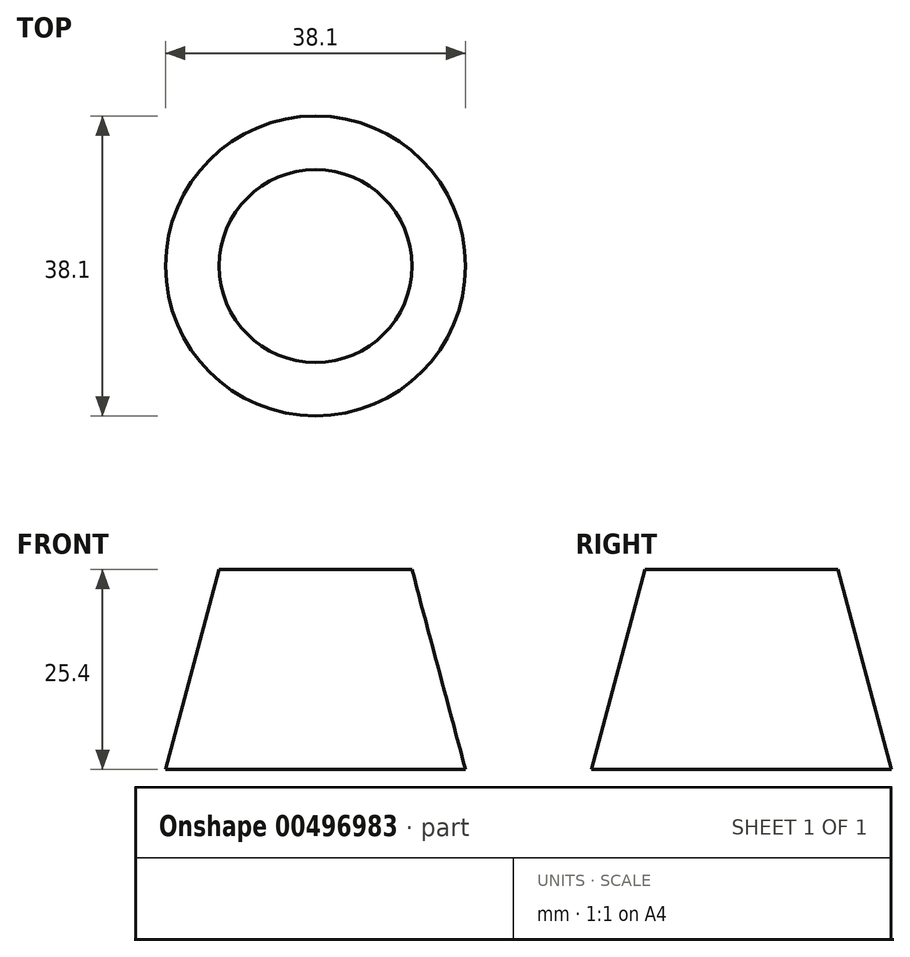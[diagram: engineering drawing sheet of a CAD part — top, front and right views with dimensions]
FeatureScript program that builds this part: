
annotation { "Feature Type Name" : "Feature", "Feature Type Description" : "" }
export const myFeature = defineFeature(function(context is Context, id is Id, definition is map)
    precondition{}
    {
        {
            var Q0;
            Q0=qCreatedBy(makeId("Top.planeOp"),FACE);
            var sketch = newSketch(context, id + "F0", { "sketchPlane" : qUnion([Q0])});
            skCircle(sketch, "E0", {"center": v(0, 0) * mm, "radius": 19.05 * mm});
            skSolve(sketch);
        }
        {
            var Q0;
            Q0 = qSketchRegion(id + "F0", true);
            extrude(context, id + "F1", {"entities" : qUnion([Q0]), "depth" : 25.4 * mm, "hasDraft" : true, "draftAngle" : 15 * degree, "draftPullDirection" : true});
        }
    });
